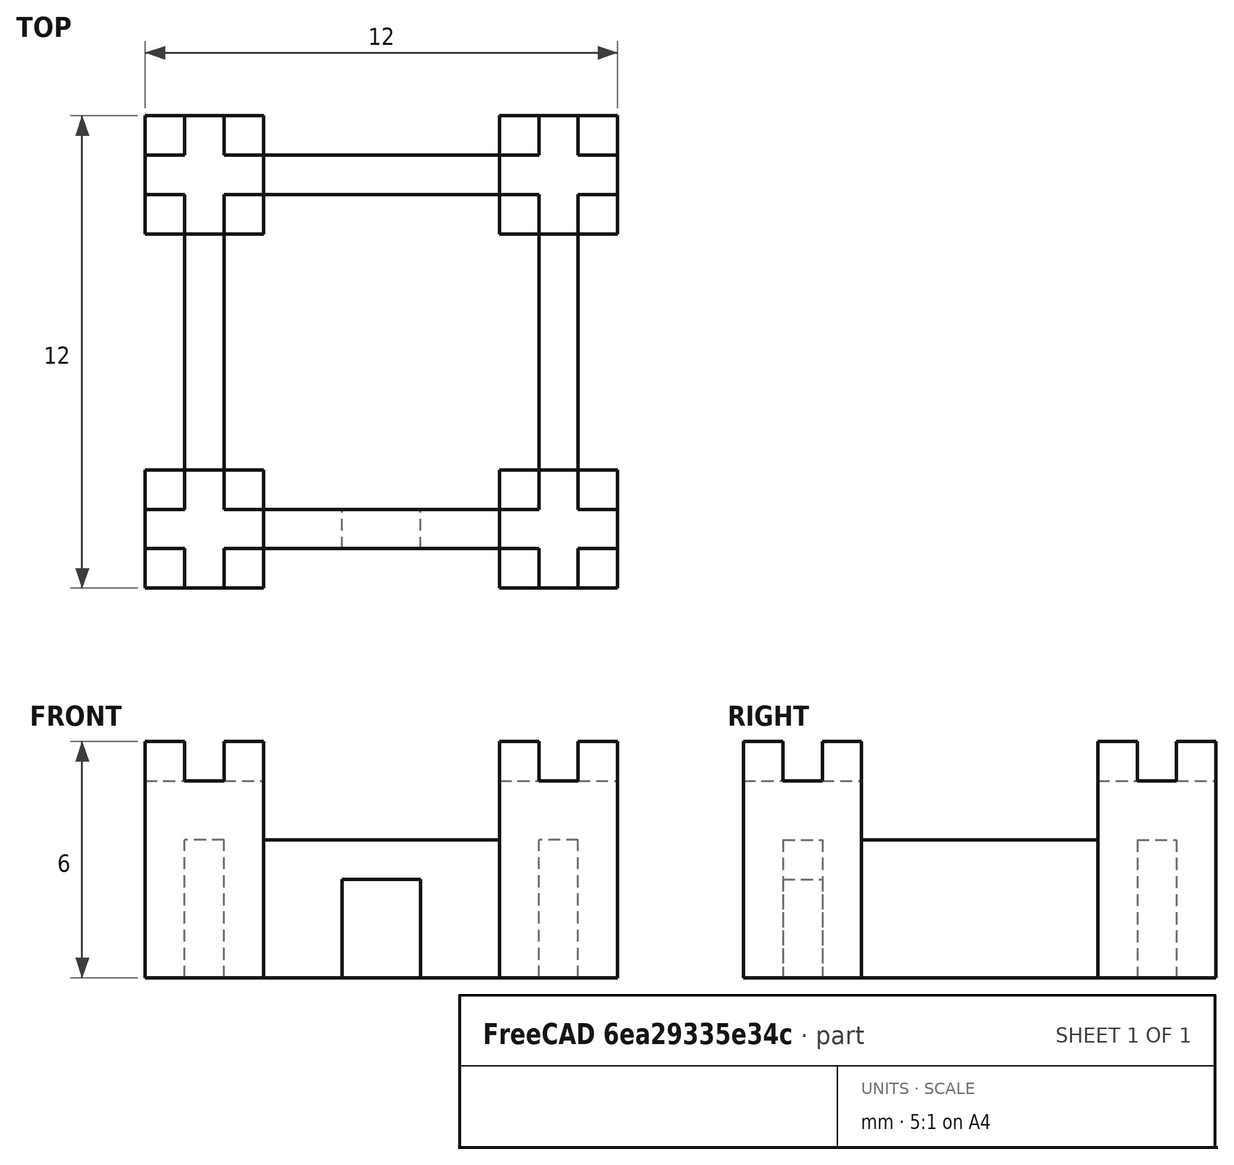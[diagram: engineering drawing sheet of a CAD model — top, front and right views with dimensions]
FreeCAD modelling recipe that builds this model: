
FCSTD DOCUMENT  (FreeCAD 0.19R)
Label: Reto 5
License: All rights reserved
LicenseURL: http://en.wikipedia.org/wiki/All_rights_reserved
objects: Part::Box×27, Part::Cut×22, App::MeasureDistance×11, Part::MultiFuse×1
note: 50 computed .brp shape members not serialized (recipe doc carries the construction recipe); baked Part::Feature solids carry a one-line shape summary decoded from their .brp

FEATURE [Part::Box] Box  label="Cubo"
  AttacherType = Attacher::AttachEngine3D
  Height = 3.5
  Length = 10
  Width = 10
FEATURE [Part::Box] Box001  label="Cubo001"
  AttacherType = Attacher::AttachEngine3D
  Height = 10
  Length = 8
  Placement = pos=(1,1,-2) rot=(0,0,1;0rad)
  Width = 8
FEATURE [Part::Cut] Cut
  Base = -> Box
  Refine = true
  Tool = -> Box001
FEATURE [Part::Box] Box002  label="Cubo002"
  AttacherType = Attacher::AttachEngine3D
  Height = 2.5
  Length = 2
  Placement = pos=(4,-3,0) rot=(0,0,1;0rad)
  Width = 10
FEATURE [Part::Cut] Cut001  label="Murallas"
  Base = -> Cut
  Refine = true
  Tool = -> Box002
FEATURE [Part::Box] Box003  label="Cubo003"
  AttacherType = Attacher::AttachEngine3D
  Height = 6
  Length = 3
  Placement = pos=(-4,0,0) rot=(0,0,1;0rad)
  Width = 3
FEATURE [Part::Box] Box005  label="Cubo005"
  AttacherType = Attacher::AttachEngine3D
  Height = 1
  Length = 1
  Placement = pos=(-3,0,5) rot=(0,0,1;0rad)
  Width = 1
FEATURE [Part::Box] Box006  label="Cubo006"
  AttacherType = Attacher::AttachEngine3D
  Height = 1
  Length = 1
  Placement = pos=(-3,2,5) rot=(0,0,1;0rad)
  Width = 1
FEATURE [Part::Box] Box007  label="Cubo007"
  AttacherType = Attacher::AttachEngine3D
  Height = 1
  Length = 1
  Placement = pos=(-3,1,5) rot=(0,0,1;0rad)
  Width = 1
FEATURE [Part::Box] Box008  label="Cubo008"
  AttacherType = Attacher::AttachEngine3D
  Height = 1
  Length = 1
  Placement = pos=(-4,1,5) rot=(0,0,1;0rad)
  Width = 1
FEATURE [Part::Box] Box009  label="Cubo009"
  AttacherType = Attacher::AttachEngine3D
  Height = 1
  Length = 1
  Placement = pos=(-2,1,5) rot=(0,0,1;0rad)
  Width = 1
FEATURE [Part::Cut] Cut002
  Base = -> Box003
  Refine = true
  Tool = -> Box005
FEATURE [Part::Cut] Cut003
  Base = -> Cut002
  Refine = true
  Tool = -> Box006
FEATURE [Part::Cut] Cut004
  Base = -> Cut003
  Refine = true
  Tool = -> Box007
FEATURE [Part::Cut] Cut005
  Base = -> Cut004
  Refine = true
  Tool = -> Box008
FEATURE [Part::Cut] Cut006  label="Torre 1"
  Base = -> Cut005
  Placement = pos=(12,-1,0) rot=(0,0,1;0rad)
  Refine = true
  Tool = -> Box009
FEATURE [Part::Box] Box010  label="Cubo010"
  AttacherType = Attacher::AttachEngine3D
  Height = 6
  Length = 3
  Placement = pos=(-4,0,0) rot=(0,0,1;0rad)
  Width = 3
FEATURE [Part::Box] Box011  label="Cubo011"
  AttacherType = Attacher::AttachEngine3D
  Height = 1
  Length = 1
  Placement = pos=(-3,0,5) rot=(0,0,1;0rad)
  Width = 1
FEATURE [Part::Box] Box012  label="Cubo012"
  AttacherType = Attacher::AttachEngine3D
  Height = 1
  Length = 1
  Placement = pos=(-3,2,5) rot=(0,0,1;0rad)
  Width = 1
FEATURE [Part::Box] Box013  label="Cubo013"
  AttacherType = Attacher::AttachEngine3D
  Height = 1
  Length = 1
  Placement = pos=(-3,1,5) rot=(0,0,1;0rad)
  Width = 1
FEATURE [Part::Box] Box014  label="Cubo014"
  AttacherType = Attacher::AttachEngine3D
  Height = 1
  Length = 1
  Placement = pos=(-4,1,5) rot=(0,0,1;0rad)
  Width = 1
FEATURE [Part::Box] Box015  label="Cubo015"
  AttacherType = Attacher::AttachEngine3D
  Height = 1
  Length = 1
  Placement = pos=(-2,1,5) rot=(0,0,1;0rad)
  Width = 1
FEATURE [Part::Cut] Cut007
  Base = -> Box010
  Refine = true
  Tool = -> Box011
FEATURE [Part::Cut] Cut008
  Base = -> Cut007
  Refine = true
  Tool = -> Box012
FEATURE [Part::Cut] Cut009
  Base = -> Cut008
  Refine = true
  Tool = -> Box013
FEATURE [Part::Cut] Cut010
  Base = -> Cut009
  Refine = true
  Tool = -> Box014
FEATURE [Part::Cut] Cut011  label="Torre 2"
  Base = -> Cut010
  Placement = pos=(3,-1,0) rot=(0,0,1;0rad)
  Refine = true
  Tool = -> Box015
FEATURE [Part::Box] Box016  label="Cubo016"
  AttacherType = Attacher::AttachEngine3D
  Height = 6
  Length = 3
  Placement = pos=(-4,0,0) rot=(0,0,1;0rad)
  Width = 3
FEATURE [Part::Box] Box017  label="Cubo017"
  AttacherType = Attacher::AttachEngine3D
  Height = 1
  Length = 1
  Placement = pos=(-3,0,5) rot=(0,0,1;0rad)
  Width = 1
FEATURE [Part::Box] Box018  label="Cubo018"
  AttacherType = Attacher::AttachEngine3D
  Height = 1
  Length = 1
  Placement = pos=(-3,2,5) rot=(0,0,1;0rad)
  Width = 1
FEATURE [Part::Box] Box019  label="Cubo019"
  AttacherType = Attacher::AttachEngine3D
  Height = 1
  Length = 1
  Placement = pos=(-3,1,5) rot=(0,0,1;0rad)
  Width = 1
FEATURE [Part::Box] Box020  label="Cubo020"
  AttacherType = Attacher::AttachEngine3D
  Height = 1
  Length = 1
  Placement = pos=(-4,1,5) rot=(0,0,1;0rad)
  Width = 1
FEATURE [Part::Box] Box021  label="Cubo021"
  AttacherType = Attacher::AttachEngine3D
  Height = 1
  Length = 1
  Placement = pos=(-2,1,5) rot=(0,0,1;0rad)
  Width = 1
FEATURE [Part::Cut] Cut012
  Base = -> Box016
  Refine = true
  Tool = -> Box017
FEATURE [Part::Cut] Cut013
  Base = -> Cut012
  Refine = true
  Tool = -> Box018
FEATURE [Part::Cut] Cut014
  Base = -> Cut013
  Refine = true
  Tool = -> Box019
FEATURE [Part::Cut] Cut015
  Base = -> Cut014
  Refine = true
  Tool = -> Box020
FEATURE [Part::Cut] Cut016  label="Torre 3"
  Base = -> Cut015
  Placement = pos=(3,8,0) rot=(0,0,1;0rad)
  Refine = true
  Tool = -> Box021
FEATURE [Part::Box] Box022  label="Cubo022"
  AttacherType = Attacher::AttachEngine3D
  Height = 6
  Length = 3
  Placement = pos=(-4,0,0) rot=(0,0,1;0rad)
  Width = 3
FEATURE [Part::Box] Box023  label="Cubo023"
  AttacherType = Attacher::AttachEngine3D
  Height = 1
  Length = 1
  Placement = pos=(-3,0,5) rot=(0,0,1;0rad)
  Width = 1
FEATURE [Part::Box] Box024  label="Cubo024"
  AttacherType = Attacher::AttachEngine3D
  Height = 1
  Length = 1
  Placement = pos=(-3,2,5) rot=(0,0,1;0rad)
  Width = 1
FEATURE [Part::Box] Box025  label="Cubo025"
  AttacherType = Attacher::AttachEngine3D
  Height = 1
  Length = 1
  Placement = pos=(-3,1,5) rot=(0,0,1;0rad)
  Width = 1
FEATURE [Part::Box] Box026  label="Cubo026"
  AttacherType = Attacher::AttachEngine3D
  Height = 1
  Length = 1
  Placement = pos=(-4,1,5) rot=(0,0,1;0rad)
  Width = 1
FEATURE [Part::Box] Box027  label="Cubo027"
  AttacherType = Attacher::AttachEngine3D
  Height = 1
  Length = 1
  Placement = pos=(-2,1,5) rot=(0,0,1;0rad)
  Width = 1
FEATURE [Part::Cut] Cut017
  Base = -> Box022
  Refine = true
  Tool = -> Box023
FEATURE [Part::Cut] Cut018
  Base = -> Cut017
  Refine = true
  Tool = -> Box024
FEATURE [Part::Cut] Cut019
  Base = -> Cut018
  Refine = true
  Tool = -> Box025
FEATURE [Part::Cut] Cut020
  Base = -> Cut019
  Refine = true
  Tool = -> Box026
FEATURE [Part::Cut] Cut021  label="Torre 4"
  Base = -> Cut020
  Placement = pos=(12,8,0) rot=(0,0,1;0rad)
  Refine = true
  Tool = -> Box027
FEATURE [App::MeasureDistance] Distance  label="Distance: 0,97 mm"
  Distance = 0.967607
  P1 = (1,10.9454,6)
  P2 = (1.9676,10.9426,6)
FEATURE [App::MeasureDistance] Distance001  label="Distance: 1,00 mm"
  Distance = 1.0005
  P1 = (8,10,5.03155)
  P2 = (8,9,5)
FEATURE [App::MeasureDistance] Distance002  label="Distance: 0,98 mm"
  Distance = 0.975399
  P1 = (7.93485,9.9754,3.5)
  P2 = (7.93372,9,3.5)
FEATURE [App::MeasureDistance] Distance004  label="Distance: 1,94 mm"
  Distance = 1.94329
  P1 = (4,0,2.5)
  P2 = (5.94329,0,2.5)
FEATURE [App::MeasureDistance] Distance005  label="Distance: 1,00 mm001"
  Distance = 1
  P1 = (6,1,0)
  P2 = (6,0,0)
FEATURE [App::MeasureDistance] Distance006  label="Distance: 6,00 mm"
  Distance = 6.00087
  P1 = (0.494647,8,5)
  P2 = (0.596801,2,5)
FEATURE [App::MeasureDistance] Distance007  label="Distance: 3,00 mm"
  Distance = 3
  P1 = (11,8,6)
  P2 = (8,8,6)
FEATURE [App::MeasureDistance] Distance008  label="Distance: 1,34 mm"
  Distance = 1.34153
  P1 = (11,0,6)
  P2 = (11,0.894266,5)
FEATURE [App::MeasureDistance] Distance009  label="Distance: 6,00 mm001"
  Distance = 6
  P1 = (-1,-1,6)
  P2 = (-1,-1,0)
FEATURE [Part::MultiFuse] Fusion  label="Reto 5"
  Refine = true
  Shapes = -> [Cut001,Cut006,Cut011,Cut016,Cut021]
FEATURE [App::MeasureDistance] Distance010  label="Distance: 3,50 mm"
  Distance = 3.50006
  P1 = (2.66033,0,3.5)
  P2 = (2.68076,0,0)
FEATURE [App::MeasureDistance] Distance011  label="Distance: 9,34 mm"
  Distance = 9.3422
  P1 = (5.03032,0,2.5)
  P2 = (5.19377,9,0)
